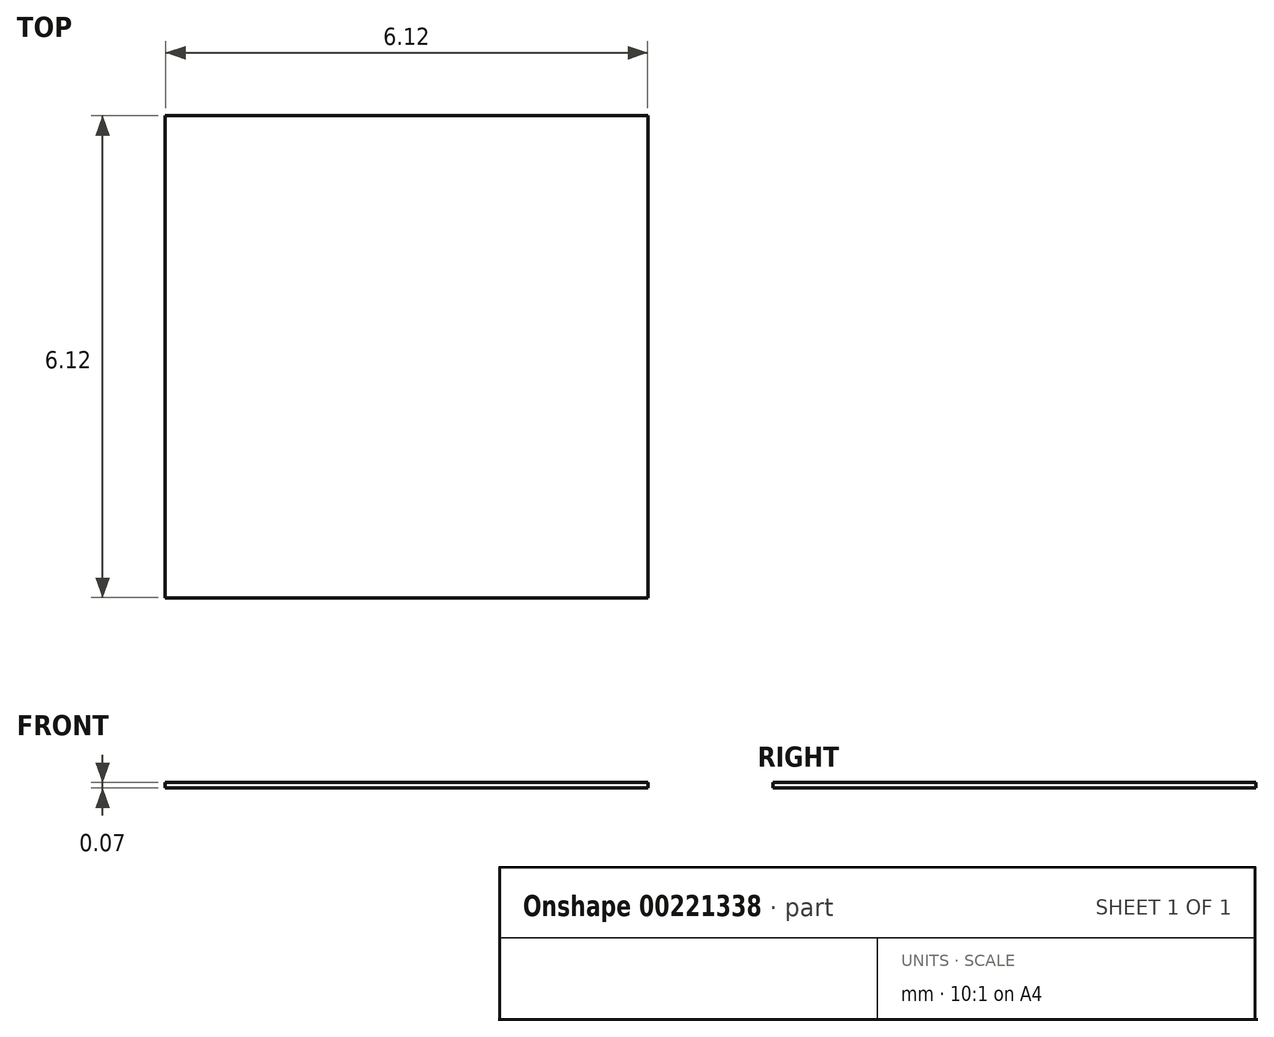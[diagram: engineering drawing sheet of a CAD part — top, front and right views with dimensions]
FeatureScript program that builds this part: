
annotation { "Feature Type Name" : "Feature", "Feature Type Description" : "" }
export const myFeature = defineFeature(function(context is Context, id is Id, definition is map)
    precondition{}
    {
        {
            var Q0;
            Q0=qCreatedBy(makeId("Top.planeOp"),FACE);
            var sketch = newSketch(context, id + "F0", { "sketchPlane" : qUnion([Q0])});
            skLineSegment(sketch, "E0.bottom", {"start": v(-3.06, -3.06) * mm, "end": v(3.06, -3.06) * mm});
            skLineSegment(sketch, "E0.top", {"start": v(-3.07, 3.06) * mm, "end": v(3.06, 3.06) * mm});
            skLineSegment(sketch, "E0.left", {"start": v(-3.06, -3.07) * mm, "end": v(-3.07, 3.06) * mm});
            skLineSegment(sketch, "E0.right", {"start": v(3.06, -3.07) * mm, "end": v(3.06, 3.06) * mm});
            skSolve(sketch);
        }
        {
            var Q0;
            Q0=makeQuery(id+"F0.imprint","IMPRINT",FACE,{"disambiguationData":[TD([[makeQuery(id+"F0.imprint","IMPRINT",EDGE,{"derivedFrom":sQuery(id+"F0.wireOp",EDGE,"E0.bottom")}),1.0]])]});
            extrude(context, id + "F1", {"entities" : qUnion([Q0]), "depth" : 0.07 * mm});
        }
    });
